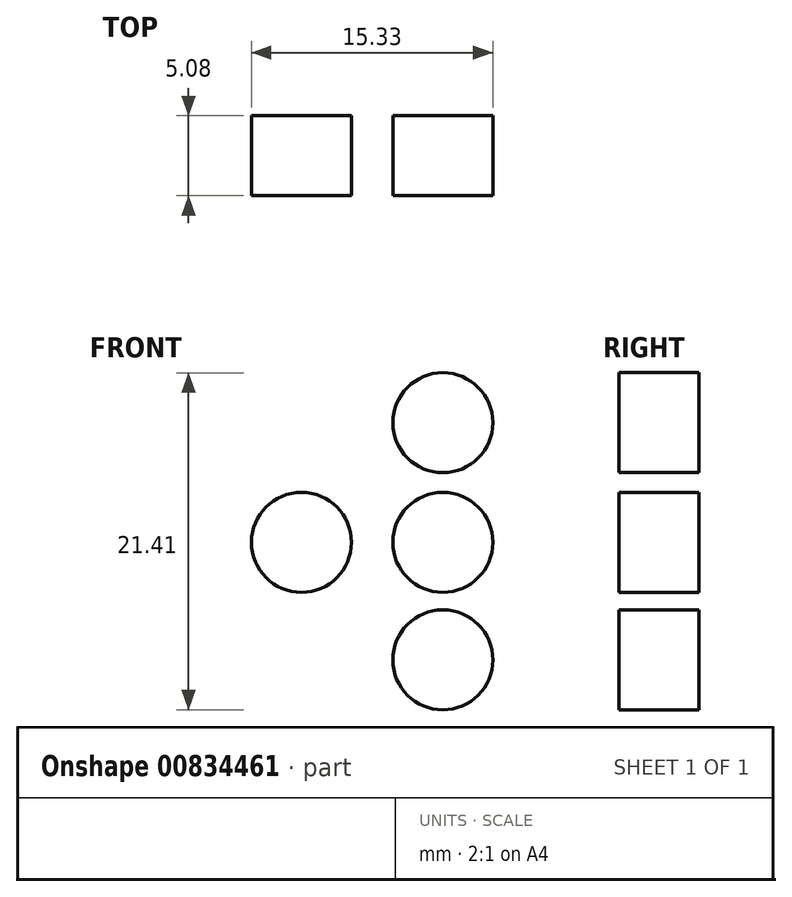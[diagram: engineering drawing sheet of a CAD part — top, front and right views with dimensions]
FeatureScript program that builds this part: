
annotation { "Feature Type Name" : "Feature", "Feature Type Description" : "" }
export const myFeature = defineFeature(function(context is Context, id is Id, definition is map)
    precondition{}
    {
        {
            var Q0;
            Q0=qCreatedBy(makeId("Front.planeOp"),FACE);
            var sketch = newSketch(context, id + "F0", { "sketchPlane" : qUnion([Q0])});
            skCircle(sketch, "E0", {"center": v(0, 0) * mm, "radius": 7.92 * mm});
            skLineSegment(sketch, "E1", {"start": v(-44.45, 0) * mm, "end": v(-25.72, 13.43) * mm});
            skLineSegment(sketch, "E2", {"start": v(-25.72, 13.43) * mm, "end": v(25.72, 13.43) * mm});
            skLineSegment(sketch, "E3", {"start": v(25.72, 13.43) * mm, "end": v(44.45, 0) * mm});
            skLineSegment(sketch, "E4", {"start": v(0, 13.43) * mm, "end": v(0, 0) * mm, "construction": true});
            skLineSegment(sketch, "E5", {"start": v(-44.45, 0) * mm, "end": v(0, 0) * mm, "construction": true});
            skLineSegment(sketch, "E6", {"start": v(0, 0) * mm, "end": v(44.45, 0) * mm, "construction": true});
            skLineSegment(sketch, "E7.MirrorCS", {"start": v(-44.45, 0) * mm, "end": v(-25.72, -13.43) * mm});
            skLineSegment(sketch, "E8.MirrorCS", {"start": v(-25.72, -13.43) * mm, "end": v(25.72, -13.43) * mm});
            skLineSegment(sketch, "E9.MirrorCS", {"start": v(25.72, -13.43) * mm, "end": v(44.45, 0) * mm});
            skSolve(sketch);
        }
        {
            var Q0;
            Q0=makeQuery(id+"F0.imprint","IMPRINT",FACE,{"disambiguationData":[TD([[makeQuery(id+"F0.imprint","IMPRINT",EDGE,{"derivedFrom":sQuery(id+"F0.wireOp",EDGE,"E0")}),-1.0]])]});
            extrude(context, id + "F1", {"entities" : qUnion([Q0]), "depth" : 5.08 * mm, "offsetDistance" : 25.4 * mm});
        }
        {
            var Q0;
            Q0=makeQuery(id+"F1.opExtrude","SWEPT_EDGE",EDGE,{"disambiguationData":[OSD([sQuery(id+"F0.wireOp",EDGE,"E3"),sQuery(id+"F0.wireOp",EDGE,"E9.MirrorCS")])]});
            var Q1;
            Q1=makeQuery(id+"F1.opExtrude","SWEPT_EDGE",EDGE,{"disambiguationData":[OSD([sQuery(id+"F0.wireOp",EDGE,"E1"),sQuery(id+"F0.wireOp",EDGE,"E7.MirrorCS")])]});
            fillet(context, id + "F2", {"entities" : qUnion([Q0, Q1]), "radius" : 1.27 * mm, "tangentPropagation" : true, "allowEdgeOverflow" : false});
        }
        {
            var Q0;
            Q0=makeQuery(id+"F1.opExtrude","CAP_FACE",FACE,{"disambiguationData":[OSD([sQuery(id+"F0.wireOp",EDGE,"E0"),sQuery(id+"F0.wireOp",EDGE,"E1"),sQuery(id+"F0.wireOp",EDGE,"E2"),sQuery(id+"F0.wireOp",EDGE,"E3"),sQuery(id+"F0.wireOp",EDGE,"E7.MirrorCS"),sQuery(id+"F0.wireOp",EDGE,"E8.MirrorCS"),sQuery(id+"F0.wireOp",EDGE,"E9.MirrorCS")])],"isStart":false});
            var sketch = newSketch(context, id + "F3", { "sketchPlane" : qUnion([Q0])});
            skCircle(sketch, "E10", {"center": v(34.6, 0) * mm, "radius": 3.18 * mm});
            skCircle(sketch, "E11", {"center": v(25.63, 0) * mm, "radius": 3.18 * mm});
            skCircle(sketch, "E12", {"center": v(25.63, 7.6) * mm, "radius": 3.18 * mm});
            skCircle(sketch, "E13", {"center": v(25.63, -7.46) * mm, "radius": 3.18 * mm});
            skLineSegment(sketch, "E14", {"start": v(0, 0) * mm, "end": v(0, 4.81) * mm, "construction": true});
            skCircle(sketch, "E15.MirrorC", {"center": v(-25.63, 7.6) * mm, "radius": 3.18 * mm});
            skCircle(sketch, "E16.MirrorC", {"center": v(-25.63, 0) * mm, "radius": 3.18 * mm});
            skCircle(sketch, "E17.MirrorC", {"center": v(-25.63, -7.46) * mm, "radius": 3.18 * mm});
            skCircle(sketch, "E18.MirrorC", {"center": v(-34.6, 0) * mm, "radius": 3.18 * mm});
            skSolve(sketch);
        }
        {
            var Q0;
            Q0=makeQuery(id+"F3.imprint","IMPRINT",FACE,{"disambiguationData":[TD([[makeQuery(id+"F3.imprint","IMPRINT",EDGE,{"derivedFrom":sQuery(id+"F3.wireOp",EDGE,"E15.MirrorC")}),-1.0]])]});
            var Q1;
            Q1=makeQuery(id+"F3.imprint","IMPRINT",FACE,{"disambiguationData":[TD([[makeQuery(id+"F3.imprint","IMPRINT",EDGE,{"derivedFrom":sQuery(id+"F3.wireOp",EDGE,"E16.MirrorC")}),-1.0]])]});
            var Q2;
            Q2=makeQuery(id+"F3.imprint","IMPRINT",FACE,{"disambiguationData":[TD([[makeQuery(id+"F3.imprint","IMPRINT",EDGE,{"derivedFrom":sQuery(id+"F3.wireOp",EDGE,"E17.MirrorC")}),-1.0]])]});
            var Q3;
            Q3=makeQuery(id+"F3.imprint","IMPRINT",FACE,{"disambiguationData":[TD([[makeQuery(id+"F3.imprint","IMPRINT",EDGE,{"derivedFrom":sQuery(id+"F3.wireOp",EDGE,"E18.MirrorC")}),-1.0]])]});
            var Q4;
            Q4=makeQuery(id+"F3.imprint","IMPRINT",FACE,{"disambiguationData":[TD([[makeQuery(id+"F3.imprint","IMPRINT",EDGE,{"derivedFrom":sQuery(id+"F3.wireOp",EDGE,"E11")}),1.0]])]});
            var Q5;
            Q5=makeQuery(id+"F3.imprint","IMPRINT",FACE,{"disambiguationData":[TD([[makeQuery(id+"F3.imprint","IMPRINT",EDGE,{"derivedFrom":sQuery(id+"F3.wireOp",EDGE,"E12")}),1.0]])]});
            var Q6;
            Q6=makeQuery(id+"F3.imprint","IMPRINT",FACE,{"disambiguationData":[TD([[makeQuery(id+"F3.imprint","IMPRINT",EDGE,{"derivedFrom":sQuery(id+"F3.wireOp",EDGE,"E10")}),1.0]])]});
            var Q7;
            Q7=makeQuery(id+"F3.imprint","IMPRINT",FACE,{"disambiguationData":[TD([[makeQuery(id+"F3.imprint","IMPRINT",EDGE,{"derivedFrom":sQuery(id+"F3.wireOp",EDGE,"E13")}),1.0]])]});
            extrude(context, id + "F4", {"entities" : qUnion([Q0, Q1, Q2, Q3, Q4, Q5, Q6, Q7]), "operationType" : NewBodyOperationType.REMOVE, "oppositeDirection" : true, "depth" : 25.4 * mm, "offsetDistance" : 25.4 * mm});
        }
    });
